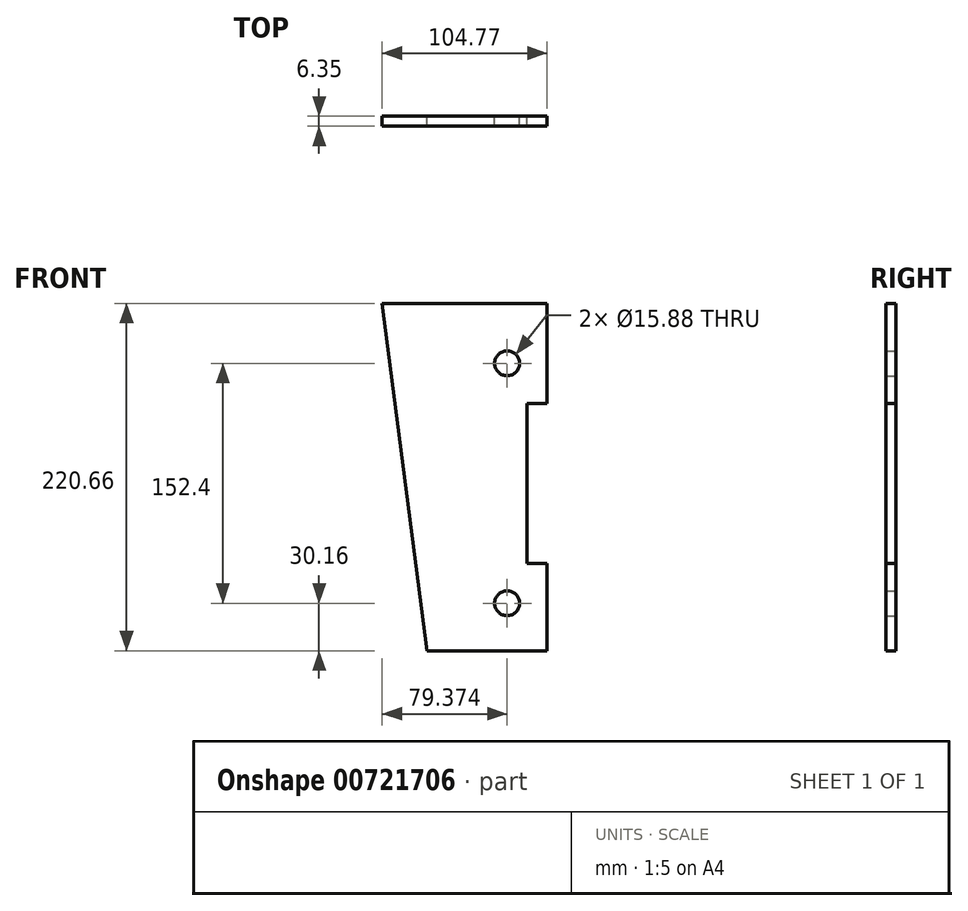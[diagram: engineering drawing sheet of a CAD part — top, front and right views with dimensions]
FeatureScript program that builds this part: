
annotation { "Feature Type Name" : "Feature", "Feature Type Description" : "" }
export const myFeature = defineFeature(function(context is Context, id is Id, definition is map)
    precondition{}
    {
        {
            var Q0;
            Q0=qCreatedBy(makeId("Front.planeOp"),FACE);
            var sketch = newSketch(context, id + "F0", { "sketchPlane" : qUnion([Q0])});
            skLineSegment(sketch, "E0", {"start": v(-18.1, 139.7) * mm, "end": v(10.48, -80.96) * mm});
            skLineSegment(sketch, "E1", {"start": v(10.48, -80.96) * mm, "end": v(86.68, -80.96) * mm});
            skLineSegment(sketch, "E2", {"start": v(86.68, -80.96) * mm, "end": v(86.68, -25.4) * mm});
            skLineSegment(sketch, "E3", {"start": v(86.68, -25.4) * mm, "end": v(73.98, -25.4) * mm});
            skLineSegment(sketch, "E4", {"start": v(73.98, 25.4) * mm, "end": v(206.22, 25.4) * mm, "construction": true});
            skLineSegment(sketch, "E5", {"start": v(73.98, 76.2) * mm, "end": v(73.98, -25.4) * mm});
            skLineSegment(sketch, "E6", {"start": v(86.68, 76.2) * mm, "end": v(86.68, 139.7) * mm});
            skLineSegment(sketch, "E7", {"start": v(86.68, 139.7) * mm, "end": v(-18.1, 139.7) * mm});
            skLineSegment(sketch, "E8.MirrorCS", {"start": v(86.68, 76.2) * mm, "end": v(73.98, 76.2) * mm});
            skLineSegment(sketch, "E9", {"start": v(61.28, -199.01) * mm, "end": v(61.28, -365.47) * mm, "construction": true});
            skCircle(sketch, "E10", {"center": v(61.28, -50.8) * mm, "radius": 7.94 * mm});
            skCircle(sketch, "E11", {"center": v(61.28, 101.6) * mm, "radius": 7.94 * mm});
            skSolve(sketch);
        }
        {
            var Q0;
            Q0=qSketchRegion(id+"F0",true);
            extrude(context, id + "F1", {"entities" : qUnion([Q0]), "depth" : 6.35 * mm, "offsetDistance" : 25.4 * mm});
        }
    });
